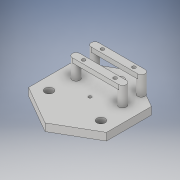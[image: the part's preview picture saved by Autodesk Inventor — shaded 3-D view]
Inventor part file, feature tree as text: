
AUTODESK INVENTOR PART (.ipt)
format: ipt  version: 2019 (Build 230136000, 136)  size: 191,488 bytes
history: native  units: mm
features: extrude x6, sketch x6
ambient origin geometry x8: Origin, YZ Plane, XZ Plane, XY Plane, X Axis, Y Axis, Z Axis, Center Point
bodies: Solid1 (feature_tree)
feature tree (12):
  extrude  "Extrusion1"  TaperAngle=150.0deg  [1 undecoded]
  extrude  "Extrusion2"  TaperAngle=90.0deg  [1 undecoded]
  extrude  "Extrusion4"  TaperAngle=120.0deg  [1 undecoded]
  extrude  "Extrusion5"  Depth=5.0mm TaperAngle=0.0deg
  extrude  "Extrusion6"  Depth=5.5mm
  extrude  "Extrusion7"  TaperAngle=30.0deg  [1 undecoded]
  sketch  "Sketch1"  dims[d0=30.0mm d1=150.0deg]
  sketch  "Sketch2"  dims[d3=30.0mm d4=90.0deg]
  sketch  "Sketch3"  dims[d5=30.0mm d6=120.0deg]
  sketch  "Sketch4"  dims[d7=25.980762mm d8=5.0mm d9=0.0mm]
  sketch  "Sketch5"  dims[d10=20.0mm d11=5.5mm]
  sketch  "Sketch6"  dims[d12=20.0mm d13=30.0deg d14=20.0mm d15=150.0deg d16=5.5mm d17=5.5mm d18=10.0mm d19=0.0mm d20=12.5mm d21=21.0mm d22=12.5mm d29=5.0mm d30=5.0mm d31=5.0mm d32=0.0mm d33=5.0mm d34=5.0mm d35=5.0mm d36=5.0mm d37=5.0mm d38=10.0mm d39=0.0mm d40=31.0mm d41=5.0mm d42=2.5mm d43=31.0mm d44=5.0mm d49=2.5mm d50=3.0mm d51=0.0mm d52=5.0mm d53=5.0mm d54=5.0mm d55=5.0mm d56=2.3mm d57=2.3mm d58=2.3mm d59=2.3mm d60=3.0mm d61=0.0mm d62=2.0mm d63=10.0mm d64=0.0mm]
note: 4 required parameter values undecoded (feature->parameter linkage not recoverable at this tier; creation-order binding heuristic only, values carry confidence <= 0.55)
